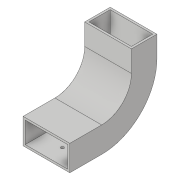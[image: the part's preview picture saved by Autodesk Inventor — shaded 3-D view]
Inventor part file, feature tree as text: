
AUTODESK INVENTOR PART (.ipt)
format: ipt  version: 2018.2 (Build 222227000, 227)  size: 111,104 bytes
history: native  units: in
note: dims shown in document units (in); Inventor stores cm internally (conversion verified against a paired STEP export)
features: sketch x4, sweep x1, extrude x1
ambient origin geometry x8: Origin, YZ Plane, XZ Plane, XY Plane, X Axis, Y Axis, Z Axis, Center Point
bodies: Solid1 (feature_tree)
feature tree (6):
  sketch  "Sketch1"  dims[d0=3.937in d1=1.9685in]
  sweep  "Sweep1"
  extrude  "Extrusion1"  Depth=2.3622in
  sketch  "Sketch2"  dims[d2=4.3307in d3=2.3622in]
  sketch  "Sketch3"  dims[d7=0.0in d8=0.0in]
  sketch  "Sketch4"  dims[d9=0.2756in d10=0.3937in d11=0.0in]
